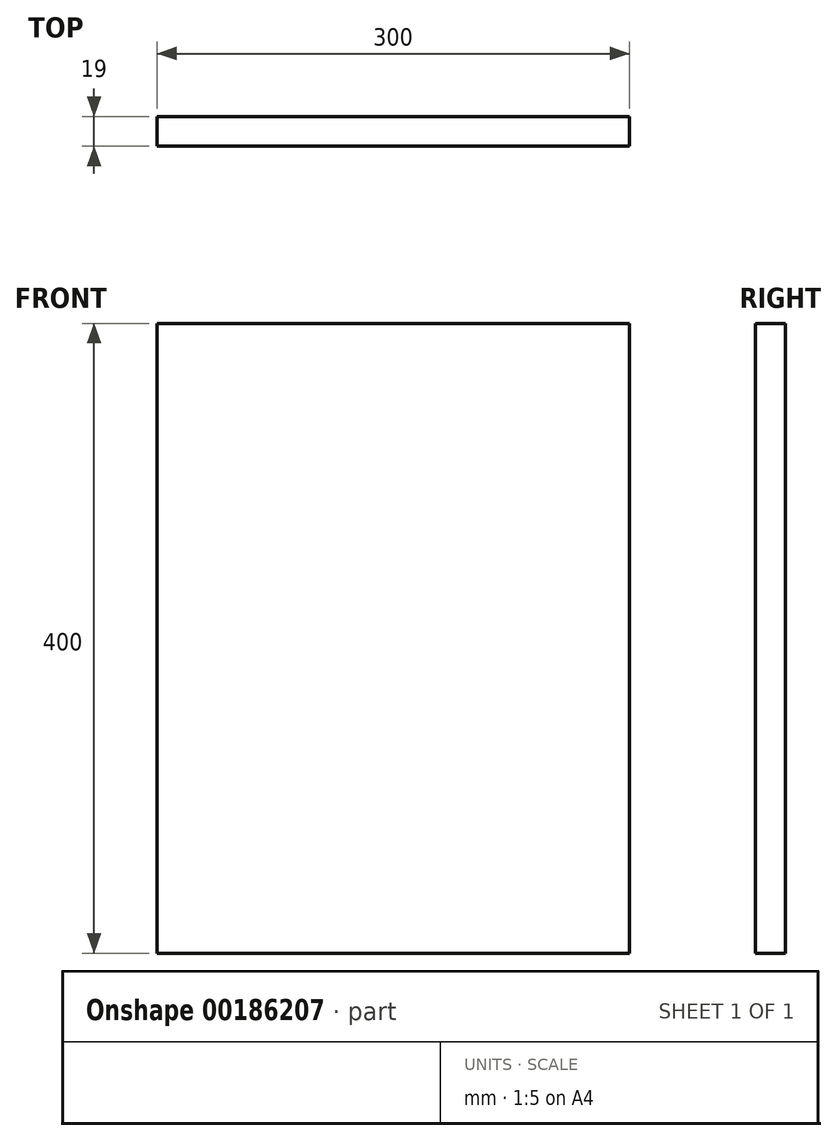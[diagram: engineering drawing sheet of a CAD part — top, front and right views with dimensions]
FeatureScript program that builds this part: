
annotation { "Feature Type Name" : "Feature", "Feature Type Description" : "" }
export const myFeature = defineFeature(function(context is Context, id is Id, definition is map)
    precondition{}
    {
        {
            var Q0;
            Q0=qCreatedBy(makeId("Front.planeOp"),FACE);
            var sketch = newSketch(context, id + "F0", { "sketchPlane" : qUnion([Q0])});
            skLineSegment(sketch, "E0.bottom", {"start": v(-149.32, 223.58) * mm, "end": v(150.68, 223.58) * mm});
            skLineSegment(sketch, "E0.top", {"start": v(-149.32, -176.42) * mm, "end": v(150.68, -176.42) * mm});
            skLineSegment(sketch, "E0.left", {"start": v(-149.32, 223.58) * mm, "end": v(-149.32, -176.42) * mm});
            skLineSegment(sketch, "E0.right", {"start": v(150.68, 223.58) * mm, "end": v(150.68, -176.42) * mm});
            skSolve(sketch);
        }
        {
            var Q0;
            Q0 = qSketchRegion(id + "F0", true);
            extrude(context, id + "F1", {"entities" : qUnion([Q0]), "depth" : 19 * mm});
        }
    });
